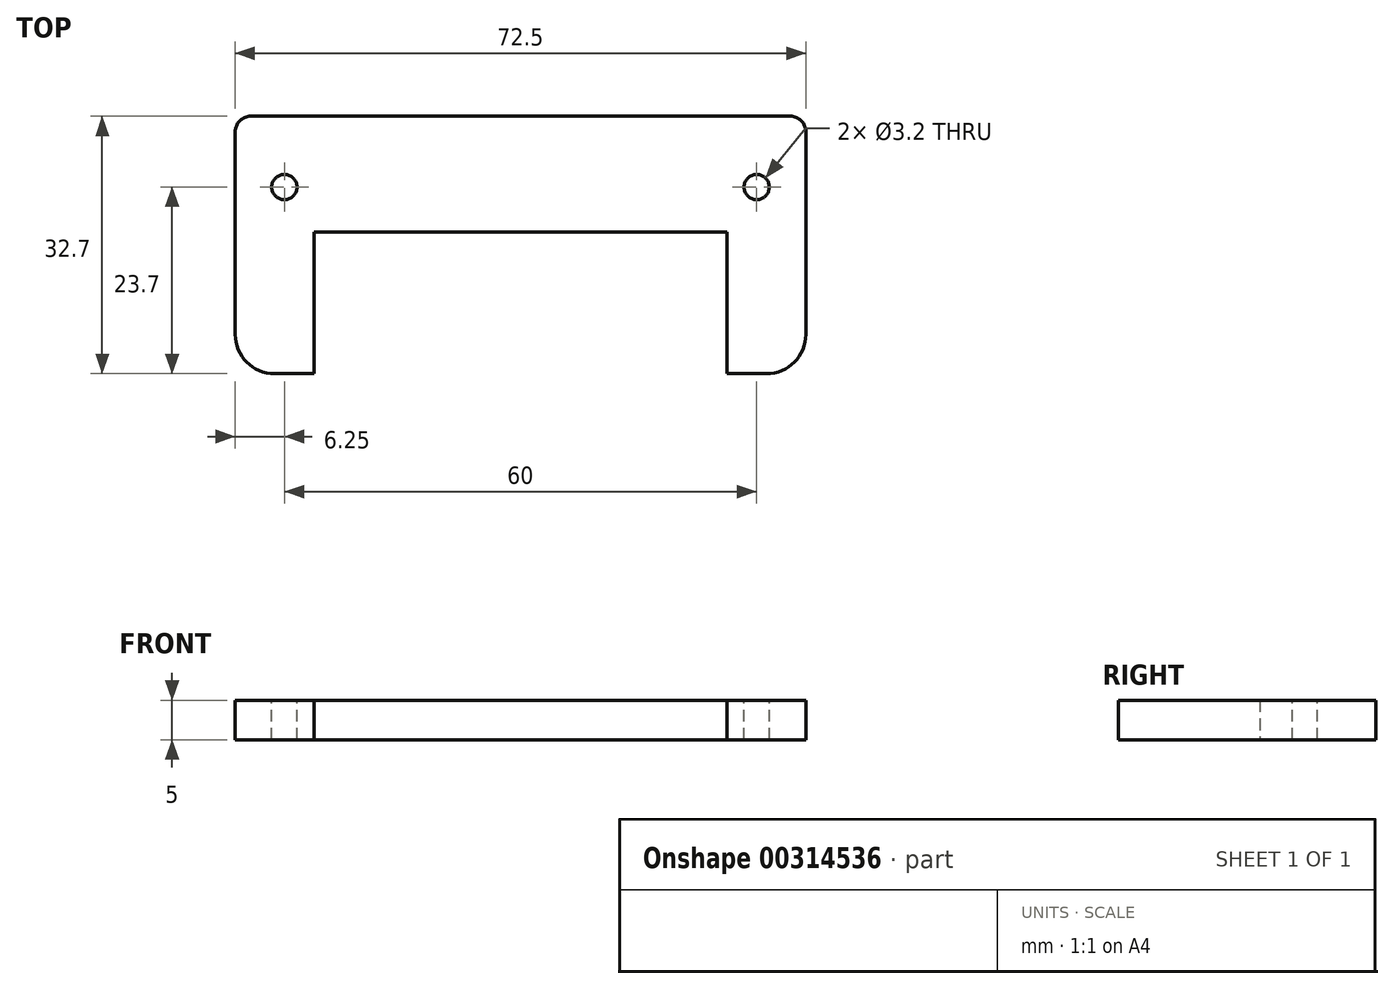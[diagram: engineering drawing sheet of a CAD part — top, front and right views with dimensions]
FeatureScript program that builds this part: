
annotation { "Feature Type Name" : "Feature", "Feature Type Description" : "" }
export const myFeature = defineFeature(function(context is Context, id is Id, definition is map)
    precondition{}
    {
        {
            var Q0;
            Q0=qCreatedBy(makeId("Top.planeOp"),FACE);
            var sketch = newSketch(context, id + "F0", { "sketchPlane" : qUnion([Q0])});
            skLineSegment(sketch, "E0.bottom", {"start": v(-36.25, -16.35) * mm, "end": v(-26.25, -16.35) * mm});
            skLineSegment(sketch, "E0.top", {"start": v(-36.25, 16.35) * mm, "end": v(36.25, 16.35) * mm});
            skLineSegment(sketch, "E0.left", {"start": v(-36.25, -16.35) * mm, "end": v(-36.25, 16.35) * mm});
            skLineSegment(sketch, "E0.right", {"start": v(36.25, -16.35) * mm, "end": v(36.25, 16.35) * mm});
            skPoint(sketch, "E0.middle", {"position": v(0, 0) * mm});
            skLineSegment(sketch, "E1.top", {"start": v(-26.25, 1.65) * mm, "end": v(26.25, 1.65) * mm});
            skLineSegment(sketch, "E1.left", {"start": v(-26.25, -16.35) * mm, "end": v(-26.25, 1.65) * mm});
            skLineSegment(sketch, "E1.right", {"start": v(26.25, -16.35) * mm, "end": v(26.25, 1.65) * mm});
            skLineSegment(sketch, "E2.trimOffspring", {"start": v(26.25, -16.35) * mm, "end": v(36.25, -16.35) * mm});
            skSolve(sketch);
        }
        {
            var Q0;
            Q0 = qSketchRegion(id + "F0", true);
            extrude(context, id + "F1", {"entities" : qUnion([Q0]), "depth" : 5 * mm});
        }
        {
            var Q0;
            Q0=makeQuery(id+"F1.opExtrude","CAP_FACE",FACE,{"disambiguationData":[OSD([sQuery(id+"F0.wireOp",EDGE,"E0.bottom"),sQuery(id+"F0.wireOp",EDGE,"E0.top"),sQuery(id+"F0.wireOp",EDGE,"E0.left"),sQuery(id+"F0.wireOp",EDGE,"E0.right"),sQuery(id+"F0.wireOp",EDGE,"E1.top"),sQuery(id+"F0.wireOp",EDGE,"E1.left"),sQuery(id+"F0.wireOp",EDGE,"E1.right"),sQuery(id+"F0.wireOp",EDGE,"E2.trimOffspring")])],"isStart":false});
            var sketch = newSketch(context, id + "F2", { "sketchPlane" : qUnion([Q0])});
            skPoint(sketch, "E3", {"position": v(-30, 7.35) * mm});
            skPoint(sketch, "E4.1.0.0", {"position": v(30, 7.35) * mm});
            skLineSegment(sketch, "E4.direction1", {"start": v(-30, 7.35) * mm, "end": v(30, 7.35) * mm, "construction": true});
            skSolve(sketch);
        }
        {
            var Q0;
            Q0=sQuery(id+"F2.wireOp",VERTEX,"E3");
            var Q1;
            Q1=sQuery(id+"F2.wireOp",VERTEX,"E4.1.0.0");
            var Q2;
            Q2=makeQuery(id+"F1.opExtrude","SWEPT_BODY",BODY,{"disambiguationData":[OSD([sQuery(id+"F0.wireOp",EDGE,"E0.bottom"),sQuery(id+"F0.wireOp",EDGE,"E0.top"),sQuery(id+"F0.wireOp",EDGE,"E0.left"),sQuery(id+"F0.wireOp",EDGE,"E0.right"),sQuery(id+"F0.wireOp",EDGE,"E1.top"),sQuery(id+"F0.wireOp",EDGE,"E1.left"),sQuery(id+"F0.wireOp",EDGE,"E1.right"),sQuery(id+"F0.wireOp",EDGE,"E2.trimOffspring")])]});
            hole(context, id + "F3", {"style" : HoleStyle.SIMPLE, "endStyle" : HoleEndStyle.BLIND, "standardTappedOrClearance" : lookupTablePath({ "standard" : "ISO", "engagement" : "75%", "pitch" : "0.75 mm", "size" : "M4", "type" : "Tapped" }), "standardBlindInLast" : lookupTablePath({ "standard" : "ISO", "engagement" : "75%", "pitch" : "0.75 mm", "size" : "M4", "type" : "Tapped" }), "holeDiameter" : 3.2 * mm, "showTappedDepth" : true, "holeDepth" : 14.25 * mm, "tappedDepth" : 12 * mm, "tapClearance" : 3, "locations" : qUnion([Q0, Q1]), "scope" : qUnion([Q2])});
        }
        {
            var Q0;
            Q0=makeQuery(id+"F1.opExtrude","SWEPT_EDGE",EDGE,{"disambiguationData":[OSD([sQuery(id+"F0.wireOp",EDGE,"E0.bottom"),sQuery(id+"F0.wireOp",EDGE,"E0.left")])]});
            var Q1;
            Q1=makeQuery(id+"F1.opExtrude","SWEPT_EDGE",EDGE,{"disambiguationData":[OSD([sQuery(id+"F0.wireOp",EDGE,"E0.right"),sQuery(id+"F0.wireOp",EDGE,"E2.trimOffspring")])]});
            fillet(context, id + "F4", {"entities" : qUnion([Q0, Q1]), "radius" : 5 * mm, "tangentPropagation" : true, "allowEdgeOverflow" : false});
        }
        {
            var Q0;
            Q0=makeQuery(id+"F1.opExtrude","SWEPT_EDGE",EDGE,{"disambiguationData":[OSD([sQuery(id+"F0.wireOp",EDGE,"E0.top"),sQuery(id+"F0.wireOp",EDGE,"E0.right")])]});
            var Q1;
            Q1=makeQuery(id+"F1.opExtrude","SWEPT_EDGE",EDGE,{"disambiguationData":[OSD([sQuery(id+"F0.wireOp",EDGE,"E0.top"),sQuery(id+"F0.wireOp",EDGE,"E0.left")])]});
            fillet(context, id + "F5", {"entities" : qUnion([Q0, Q1]), "radius" : 2 * mm, "tangentPropagation" : true, "allowEdgeOverflow" : false});
        }
    });
